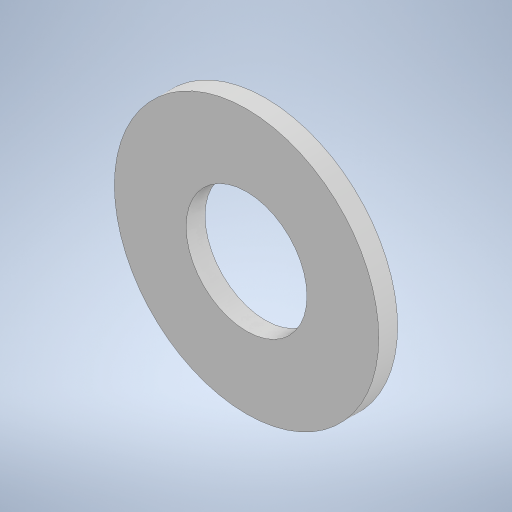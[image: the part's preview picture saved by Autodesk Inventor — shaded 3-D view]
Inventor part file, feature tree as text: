
AUTODESK INVENTOR PART (.ipt)
format: ipt  version: 2023 (Build 270158000, 158)  size: 237,568 bytes
history: native  units: in
note: dims shown in document units (in); Inventor stores cm internally (conversion verified against a paired STEP export)
features: extrude x1, sketch x1
ambient origin geometry x8: Origin, YZ Plane, XZ Plane, XY Plane, X Axis, Y Axis, Z Axis, Center Point
bodies: Solid1 (feature_tree)
feature tree (2):
  extrude  "Extrusion1"  Depth=0.0197in
  sketch  "Sketch1"  dims[d0=0.126in d1=0.2756in d2=0.0197in d3=0.0in d4=0.0in d5=0.0in d6=0.0in d7=0.0in]
